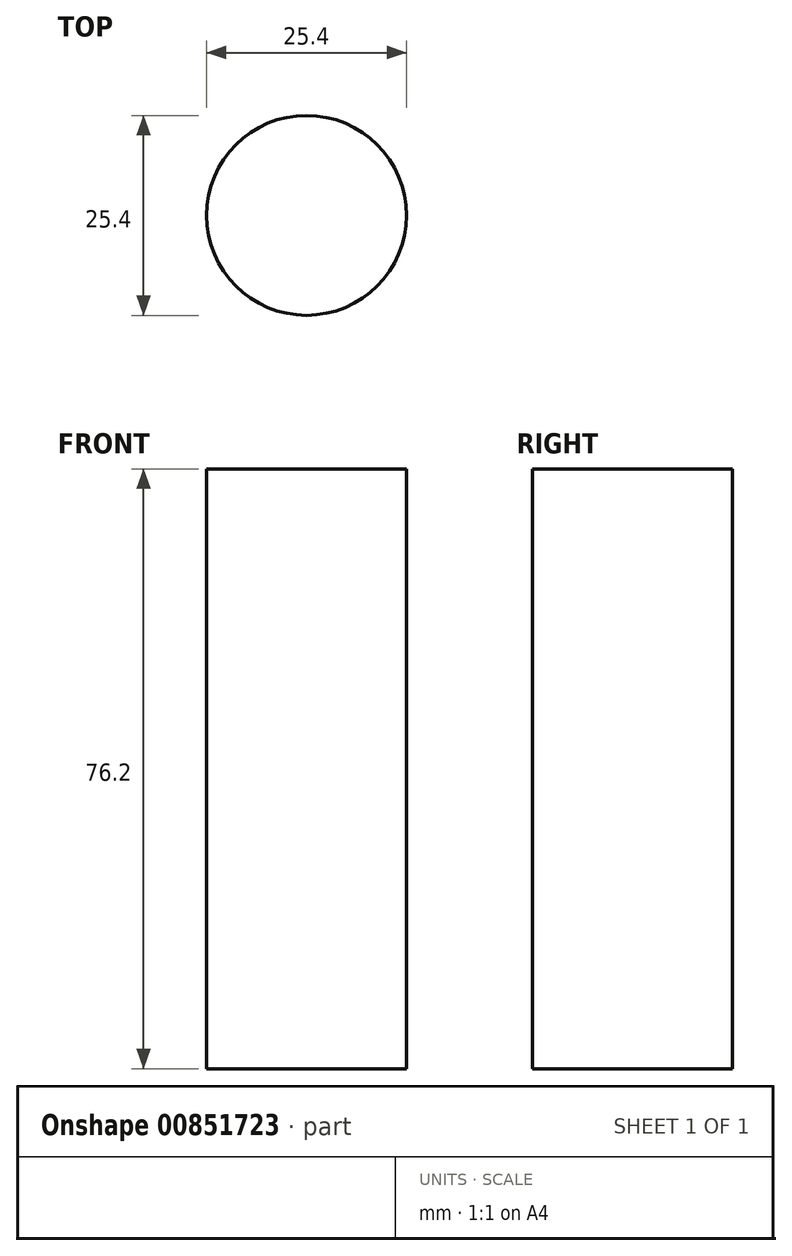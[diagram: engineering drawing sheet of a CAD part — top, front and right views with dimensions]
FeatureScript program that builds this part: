
annotation { "Feature Type Name" : "Feature", "Feature Type Description" : "" }
export const myFeature = defineFeature(function(context is Context, id is Id, definition is map)
    precondition{}
    {
        {
            var Q0;
            Q0=qCreatedBy(makeId("Top.planeOp"),FACE);
            var sketch = newSketch(context, id + "F0", { "sketchPlane" : qUnion([Q0])});
            skCircle(sketch, "E0", {"center": v(0, 0) * mm, "radius": 12.7 * mm});
            skSolve(sketch);
        }
        {
            var Q0;
            Q0=makeQuery(id+"F0.imprint","IMPRINT",FACE,{"disambiguationData":[TD([[makeQuery(id+"F0.imprint","IMPRINT",EDGE,{"derivedFrom":sQuery(id+"F0.wireOp",EDGE,"E0")}),1.0]])]});
            extrude(context, id + "F1", {"entities" : qUnion([Q0]), "depth" : 76.2 * mm, "offsetDistance" : 25.4 * mm});
        }
    });
